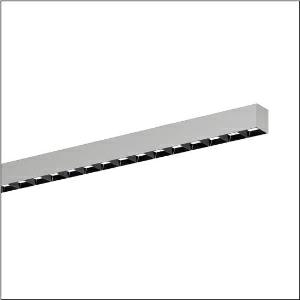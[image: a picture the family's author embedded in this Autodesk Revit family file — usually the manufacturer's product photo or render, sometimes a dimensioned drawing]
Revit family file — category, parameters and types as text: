
# Revit family: silica_r__21_51mx21tctas_c3b1
name_source: partatom
category: Lighting Fixtures
units: mm (PartAtom-declared; Revit-internal decimal feet)

## family parameters
Cut with Voids When Loaded = No
Host = Face
Light Source = No
Part Type = Normal
Room Calculation Point = No
Round Connector Dimension = Use Diameter
Shared = No

## types (1)
- --- (1 x LED, 9300 lm, 80.5 W, 6500K)
    Apparent Load = 81 VA
    CIE Flux Codes = 85 99 100 100 100
    Color Rendering = 80
    Color Temperature = 6500K
    Default Elevation = 1800 mm
    Description = Silica® 21, office luminaire, primary light control with darklight reflector, of PMMA, black, CAT 2 (L<= 3000cd/m²), light emission: direct distribution, primary light characteristic: symmetric, installation type: surface-mounted, LED, rated luminous flux: 9.300lm, luminous efficacy: 110lm/W, light colour: 8tw, colour temperature: 2700..6500K, control gear: ECG DALI, with terminal, 3+2-pole, max. 2.5mm², mains connection: 220..240V, AC, 50/60Hz, rated input power: 84.6W, luminaire housing, of aluminium, metallic grey (RAL 9006), length: 3.004mm, width: 53mm, height: 53mm, protection rating (complete): IP20, insulation class (complete): insulation class I (protective earthing), certification: CE, permissible operating ambient temperature: 0..+35°C, standard: EN 50419, packaging unit: 1 piece
    Height = 0 mm  [stored 0 ft]
    Lamp = 1 x LED
    Lamp Light Flux = 9300 lm
    Lamp Power = 80.5 W
    Lamp count = 1
    Length = 3004 mm
    Luminous efficacy = 116 lm/W
    Manufacturer = Siteco
    ModVariant = No
    Model = 51MX21TCTAS
    Mounting Place = Ceiling
    Mounting Type = Recessed
    Number of Poles = 1
    OnlyDefault = Yes
    Power Factor = 1
    Product Name = Silica® 21
    Product group = office luminaire | ceiling recessed
    ProductGroupID = 400
    Protection Class = Protection class I
    Protection Degree = IP 20
    RLX_Detail_Level = 1
    RLX_Emergency_Light_Flux = 0 lm
    RLX_Emergency_Type = 0
    RLX_Emergency_Type_DB = No
    RlxData = <blob elided: 60709 chars, md5=67ac7163>
    Socket = socket
    Standby Power = 0 W
    System Light Flux = 9300 lm
    System Power = 81 W
    Type Comments = individual setting
    Type Image = l_1335929.jpg
    URL = http://relux.com
    VarID = @adj_109843
    Voltage = 0 V
    Weight = 0.00 kg
    Width = 53 mm

note: [stored X ft] marks values corroborated as IEEE doubles in the binary element streams (Revit-internal decimal feet)

## geometry (parser evidence)
native form markers: Blend x4, Sweep x13
no freeform markers — native parametric forms only
